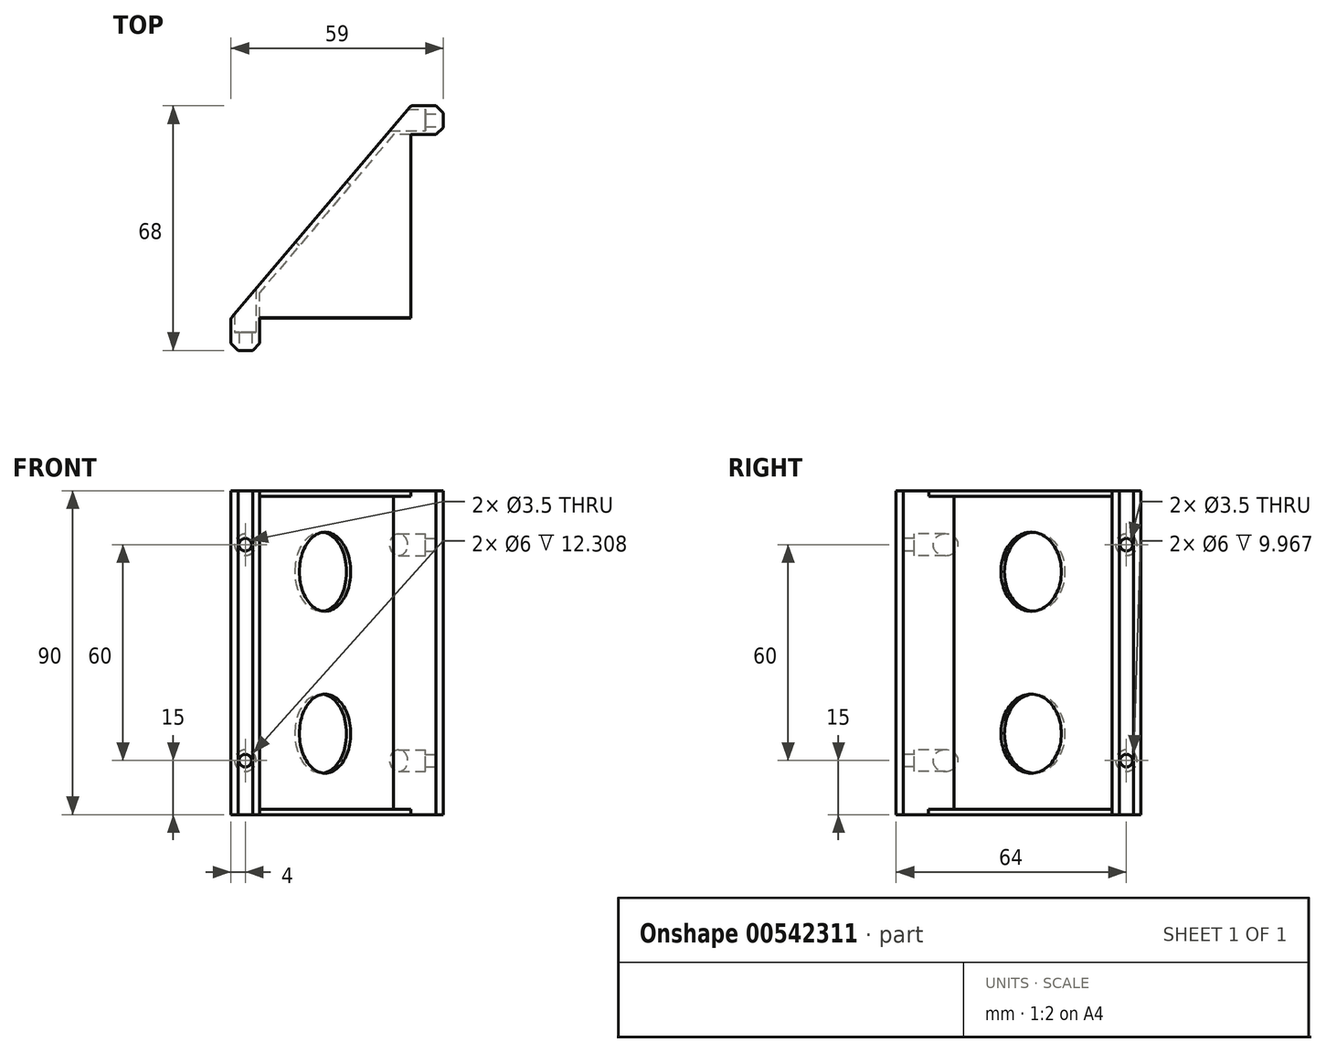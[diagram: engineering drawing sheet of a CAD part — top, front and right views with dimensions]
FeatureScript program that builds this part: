
annotation { "Feature Type Name" : "Feature", "Feature Type Description" : "" }
export const myFeature = defineFeature(function(context is Context, id is Id, definition is map)
    precondition{}
    {
        {
            var Q0;
            Q0=qCreatedBy(makeId("Top.planeOp"),FACE);
            var sketch = newSketch(context, id + "F0", { "sketchPlane" : qUnion([Q0])});
            skLineSegment(sketch, "E0.bottom", {"start": v(0, 0) * mm, "end": v(30, 0) * mm, "construction": true});
            skLineSegment(sketch, "E0.top", {"start": v(0, 30) * mm, "end": v(11, 30) * mm, "construction": true});
            skLineSegment(sketch, "E0.left", {"start": v(0, 0) * mm, "end": v(0, 30) * mm, "construction": true});
            skLineSegment(sketch, "E0.right", {"start": v(30, 0) * mm, "end": v(30, 30) * mm, "construction": true});
            skLineSegment(sketch, "E1.bottom", {"start": v(61, 70) * mm, "end": v(91, 70) * mm, "construction": true});
            skLineSegment(sketch, "E1.top", {"start": v(61, 100) * mm, "end": v(91, 100) * mm, "construction": true});
            skLineSegment(sketch, "E1.left", {"start": v(61, 70) * mm, "end": v(61, 81) * mm, "construction": true});
            skLineSegment(sketch, "E1.right", {"start": v(91, 70) * mm, "end": v(91, 100) * mm, "construction": true});
            skLineSegment(sketch, "E2", {"start": v(91, 100) * mm, "end": v(61, 100) * mm, "construction": true});
            skLineSegment(sketch, "E3", {"start": v(0, 30) * mm, "end": v(0, 0) * mm, "construction": true});
            skLineSegment(sketch, "E4.bottom", {"start": v(61, 89) * mm, "end": v(70, 89) * mm});
            skLineSegment(sketch, "E4.top", {"start": v(61, 81) * mm, "end": v(70, 81) * mm});
            skLineSegment(sketch, "E4.left", {"start": v(61, 89) * mm, "end": v(61, 87.45) * mm});
            skLineSegment(sketch, "E4.right", {"start": v(70, 89) * mm, "end": v(70, 81) * mm});
            skLineSegment(sketch, "E5.top", {"start": v(11, 21) * mm, "end": v(19, 21) * mm});
            skLineSegment(sketch, "E5.left", {"start": v(11, 30) * mm, "end": v(11, 21) * mm});
            skLineSegment(sketch, "E5.right", {"start": v(19, 30) * mm, "end": v(19, 21) * mm});
            skPoint(sketch, "E6.end.orphan", {"position": v(19, 30) * mm});
            skPoint(sketch, "E6.start.orphan", {"position": v(61, 81) * mm});
            skLineSegment(sketch, "E7", {"start": v(19, 30) * mm, "end": v(19, 33.33) * mm});
            skLineSegment(sketch, "E8", {"start": v(61, 81) * mm, "end": v(56.19, 81) * mm});
            skLineSegment(sketch, "E9.trimOffspring", {"start": v(61, 84.36) * mm, "end": v(61, 100) * mm, "construction": true});
            skLineSegment(sketch, "E10.trimOffspring", {"start": v(19, 30) * mm, "end": v(30, 30) * mm, "construction": true});
            skLineSegment(sketch, "E11", {"start": v(61, 89) * mm, "end": v(11, 30) * mm});
            skLineSegment(sketch, "E12", {"start": v(19, 33.33) * mm, "end": v(19, 37.12) * mm});
            skLineSegment(sketch, "E13", {"start": v(56.19, 81) * mm, "end": v(19, 37.12) * mm});
            skPoint(sketch, "E14.orphan", {"position": v(12.97, 30) * mm});
            skLineSegment(sketch, "E15.trimOffspring", {"start": v(13.71, 30) * mm, "end": v(16.26, 30) * mm, "construction": true});
            skLineSegment(sketch, "E16.trimOffspring", {"start": v(61, 87.45) * mm, "end": v(61, 100) * mm, "construction": true});
            skSolve(sketch);
        }
        {
            var Q0;
            Q0 = qSketchRegion(id + "F0", true);
            extrude(context, id + "F1", {"entities" : qUnion([Q0]), "depth" : 90 * mm, "offsetDistance" : 25 * mm});
        }
        {
            var Q0;
            Q0=makeQuery(id+"F1.opExtrude","SWEPT_FACE",FACE,{"disambiguationData":[OSD([sQuery(id+"F0.wireOp",EDGE,"E11")])]});
            var sketch = newSketch(context, id + "F2", { "sketchPlane" : qUnion([Q0])});
            skLineSegment(sketch, "E17", {"start": v(-68.67, 90) * mm, "end": v(-68.67, -32.24) * mm, "construction": true});
            skCircle(sketch, "E18", {"center": v(-68.67, 67.5) * mm, "radius": 11 * mm});
            skCircle(sketch, "E19", {"center": v(-68.67, 22.5) * mm, "radius": 11 * mm});
            skLineSegment(sketch, "E20", {"start": v(-30, 45) * mm, "end": v(-110.72, 45) * mm, "construction": true});
            skSolve(sketch);
        }
        {
            var Q0;
            Q0 = qSketchRegion(id + "F2", true);
            extrude(context, id + "F3", {"entities" : qUnion([Q0]), "operationType" : NewBodyOperationType.REMOVE, "oppositeDirection" : true, "depth" : 25 * mm, "offsetDistance" : 25 * mm});
        }
        {
            var Q0;
            Q0=makeQuery(id+"F1.opExtrude","SWEPT_FACE",FACE,{"disambiguationData":[OSD([sQuery(id+"F0.wireOp",EDGE,"E5.top")])]});
            var sketch = newSketch(context, id + "F4", { "sketchPlane" : qUnion([Q0])});
            skLineSegment(sketch, "E21", {"start": v(15, 90) * mm, "end": v(15, 0) * mm});
            skCircle(sketch, "E22", {"center": v(15, 75) * mm, "radius": 1.75 * mm});
            skCircle(sketch, "E23", {"center": v(15, 15) * mm, "radius": 1.75 * mm});
            skSolve(sketch);
        }
        {
            var Q0;
            Q0 = qSketchRegion(id + "F4", true);
            extrude(context, id + "F5", {"entities" : qUnion([Q0]), "operationType" : NewBodyOperationType.REMOVE, "oppositeDirection" : true, "depth" : 25 * mm, "offsetDistance" : 25 * mm});
        }
        {
            var Q0;
            Q0=makeQuery(id+"F1.opExtrude","SWEPT_FACE",FACE,{"disambiguationData":[OSD([sQuery(id+"F0.wireOp",EDGE,"E4.right")])]});
            var sketch = newSketch(context, id + "F6", { "sketchPlane" : qUnion([Q0])});
            skCircle(sketch, "E24", {"center": v(85, 75) * mm, "radius": 1.75 * mm});
            skPoint(sketch, "E24.centerSnap0", {"position": v(85, 90) * mm});
            skCircle(sketch, "E25", {"center": v(85, 15) * mm, "radius": 1.75 * mm});
            skSolve(sketch);
        }
        {
            var Q0;
            Q0 = qSketchRegion(id + "F6", true);
            extrude(context, id + "F7", {"entities" : qUnion([Q0]), "operationType" : NewBodyOperationType.REMOVE, "oppositeDirection" : true, "depth" : 25 * mm, "offsetDistance" : 25 * mm});
        }
        {
            var Q0;
            Q0=makeQuery(id+"F1.opExtrude","SWEPT_FACE",FACE,{"disambiguationData":[OSD([sQuery(id+"F0.wireOp",EDGE,"E4.right")])]});
            cPlane(context, id + "F8", {"entities" : qUnion([Q0]), "cplaneType" : CPlaneType.OFFSET, "offset" : 5 * mm, "oppositeDirection" : true, "width" : 150 * mm, "height" : 150 * mm});
        }
        {
            var Q0;
            Q0=qCreatedBy(id+"F8.planeOp",FACE);
            var sketch = newSketch(context, id + "F9", { "sketchPlane" : qUnion([Q0])});
            skCircle(sketch, "E26", {"center": v(85, 75) * mm, "radius": 3 * mm});
            skCircle(sketch, "E27", {"center": v(85, 15) * mm, "radius": 3 * mm});
            skSolve(sketch);
        }
        {
            var Q0;
            Q0 = qSketchRegion(id + "F9", true);
            extrude(context, id + "F10", {"entities" : qUnion([Q0]), "operationType" : NewBodyOperationType.REMOVE, "oppositeDirection" : true, "depth" : 25 * mm, "offsetDistance" : 25 * mm});
        }
        {
            var Q0;
            Q0=makeQuery(id+"F1.opExtrude","SWEPT_FACE",FACE,{"disambiguationData":[OSD([sQuery(id+"F0.wireOp",EDGE,"E5.top")])]});
            cPlane(context, id + "F11", {"entities" : qUnion([Q0]), "cplaneType" : CPlaneType.OFFSET, "offset" : 5 * mm, "oppositeDirection" : true, "width" : 150 * mm, "height" : 150 * mm});
        }
        {
            var Q0;
            Q0=qCreatedBy(id+"F11.planeOp",FACE);
            var sketch = newSketch(context, id + "F12", { "sketchPlane" : qUnion([Q0])});
            skCircle(sketch, "E28", {"center": v(15, 75) * mm, "radius": 3 * mm});
            skCircle(sketch, "E29", {"center": v(15, 15) * mm, "radius": 3 * mm});
            skSolve(sketch);
        }
        {
            var Q0;
            Q0 = qSketchRegion(id + "F12", true);
            extrude(context, id + "F13", {"entities" : qUnion([Q0]), "operationType" : NewBodyOperationType.REMOVE, "oppositeDirection" : true, "depth" : 25 * mm, "offsetDistance" : 25 * mm});
        }
        {
            var Q0;
            Q0=makeQuery(id+"F1.opExtrude","SWEPT_EDGE",EDGE,{"disambiguationData":[OSD([sQuery(id+"F0.wireOp",EDGE,"E4.top"),sQuery(id+"F0.wireOp",EDGE,"E4.right")])]});
            var Q1;
            Q1=makeQuery(id+"F1.opExtrude","SWEPT_EDGE",EDGE,{"disambiguationData":[OSD([sQuery(id+"F0.wireOp",EDGE,"E4.bottom"),sQuery(id+"F0.wireOp",EDGE,"E4.right")])]});
            var Q2;
            Q2=makeQuery(id+"F1.opExtrude","SWEPT_EDGE",EDGE,{"disambiguationData":[OSD([sQuery(id+"F0.wireOp",EDGE,"E5.top"),sQuery(id+"F0.wireOp",EDGE,"E5.right")])]});
            var Q3;
            Q3=makeQuery(id+"F1.opExtrude","SWEPT_EDGE",EDGE,{"disambiguationData":[OSD([sQuery(id+"F0.wireOp",EDGE,"E5.top"),sQuery(id+"F0.wireOp",EDGE,"E5.left")])]});
            chamfer(context, id + "F14", {"entities" : qUnion([Q0, Q1, Q2, Q3]), "width" : 2 * mm, "tangentPropagation" : true});
        }
        {
            var Q0;
            Q0=makeQuery(id+"F1.opExtrude","SWEPT_EDGE",EDGE,{"disambiguationData":[OSD([sQuery(id+"F0.wireOp",EDGE,"E4.bottom"),sQuery(id+"F0.wireOp",EDGE,"E11")])]});
            var Q1;
            Q1=makeQuery(id+"F1.opExtrude","SWEPT_EDGE",EDGE,{"disambiguationData":[OSD([sQuery(id+"F0.wireOp",EDGE,"E5.left"),sQuery(id+"F0.wireOp",EDGE,"E11")])]});
            fillet(context, id + "F15", {"entities" : qUnion([Q0, Q1]), "radius" : 1 * mm, "tangentPropagation" : true, "allowEdgeOverflow" : false});
        }
        {
            var Q0;
            Q0=makeQuery(id+"F1.opExtrude","CAP_FACE",FACE,{"disambiguationData":[OSD([sQuery(id+"F0.wireOp",EDGE,"E4.bottom"),sQuery(id+"F0.wireOp",EDGE,"E4.top"),sQuery(id+"F0.wireOp",EDGE,"E4.right"),sQuery(id+"F0.wireOp",EDGE,"E5.top"),sQuery(id+"F0.wireOp",EDGE,"E5.left"),sQuery(id+"F0.wireOp",EDGE,"E5.right"),sQuery(id+"F0.wireOp",EDGE,"E7"),sQuery(id+"F0.wireOp",EDGE,"E8"),sQuery(id+"F0.wireOp",EDGE,"E11"),sQuery(id+"F0.wireOp",EDGE,"E12"),sQuery(id+"F0.wireOp",EDGE,"E13")])],"isStart":false});
            var sketch = newSketch(context, id + "F16", { "sketchPlane" : qUnion([Q0])});
            skLineSegment(sketch, "E30", {"start": v(19, 30.06) * mm, "end": v(61, 30.06) * mm});
            skPoint(sketch, "E31.startSnap0", {"position": v(62.1, 81) * mm});
            skLineSegment(sketch, "E32", {"start": v(61, 81) * mm, "end": v(61, 30.06) * mm});
            skLineSegment(sketch, "E33", {"start": v(61, 81) * mm, "end": v(56.19, 81) * mm});
            skLineSegment(sketch, "E34", {"start": v(56.19, 81) * mm, "end": v(19, 37.12) * mm});
            skLineSegment(sketch, "E35", {"start": v(19, 37.12) * mm, "end": v(19, 30.06) * mm});
            skSolve(sketch);
        }
        {
            var Q0;
            Q0 = qSketchRegion(id + "F16", true);
            extrude(context, id + "F17", {"entities" : qUnion([Q0]), "operationType" : NewBodyOperationType.ADD, "oppositeDirection" : true, "depth" : 1.5 * mm, "offsetDistance" : 25 * mm});
        }
        {
            var Q0;
            Q0=makeQuery(id+"F0.imprint","IMPRINT",FACE,{"disambiguationData":[TD([[makeQuery(id+"F0.imprint","IMPRINT",EDGE,{"derivedFrom":sQuery(id+"F0.wireOp",EDGE,"E4.bottom")}),-1.0]])]});
            var sketch = newSketch(context, id + "F18", { "sketchPlane" : qUnion([Q0])});
            skLineSegment(sketch, "E36", {"start": v(61, 81) * mm, "end": v(61, 30) * mm});
            skLineSegment(sketch, "E37", {"start": v(19, 30) * mm, "end": v(61, 30) * mm});
            skLineSegment(sketch, "E38", {"start": v(19, 30) * mm, "end": v(19, 37.12) * mm});
            skLineSegment(sketch, "E39", {"start": v(19, 37.12) * mm, "end": v(56.19, 81) * mm});
            skLineSegment(sketch, "E40", {"start": v(56.19, 81) * mm, "end": v(61, 81) * mm});
            skSolve(sketch);
        }
        {
            var Q0;
            Q0 = qSketchRegion(id + "F18", true);
            extrude(context, id + "F19", {"entities" : qUnion([Q0]), "operationType" : NewBodyOperationType.ADD, "depth" : 1.5 * mm, "offsetDistance" : 25 * mm});
        }
    });
